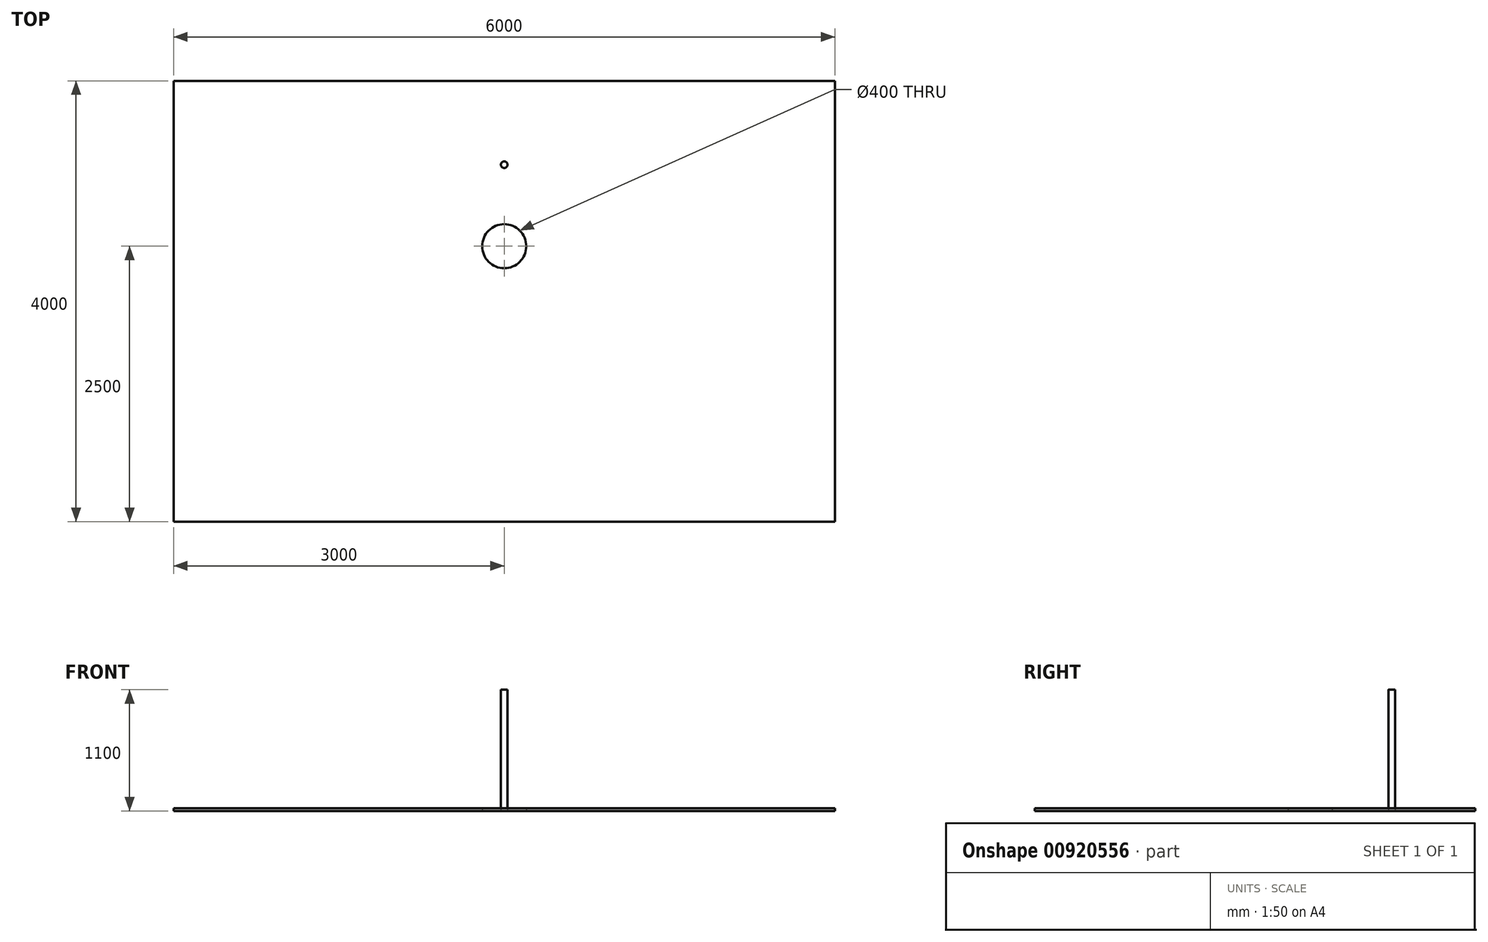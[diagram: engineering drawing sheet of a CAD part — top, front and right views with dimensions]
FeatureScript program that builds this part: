
annotation { "Feature Type Name" : "Feature", "Feature Type Description" : "" }
export const myFeature = defineFeature(function(context is Context, id is Id, definition is map)
    precondition{}
    {
        {
            var Q0;
            Q0=qCreatedBy(makeId("Top.planeOp"),FACE);
            var sketch = newSketch(context, id + "F0", { "sketchPlane" : qUnion([Q0])});
            skLineSegment(sketch, "E0.bottom", {"start": v(-3000, -3300) * mm, "end": v(3000, -3300) * mm});
            skLineSegment(sketch, "E0.top", {"start": v(-3000, 700) * mm, "end": v(3000, 700) * mm});
            skLineSegment(sketch, "E0.left", {"start": v(-3000, -3300) * mm, "end": v(-3000, 700) * mm});
            skLineSegment(sketch, "E0.right", {"start": v(3000, -3300) * mm, "end": v(3000, 700) * mm});
            skCircle(sketch, "E1", {"center": v(0, -800) * mm, "radius": 200 * mm});
            skSolve(sketch);
        }
        {
            var Q0;
            Q0 = qSketchRegion(id + "F0", true);
            extrude(context, id + "F1", {"entities" : qUnion([Q0]), "depth" : 25 * mm, "offsetDistance" : 25 * mm});
        }
        {
            var Q0;
            Q0=makeQuery(id+"F0.imprint","IMPRINT",FACE,{"disambiguationData":[TD([[makeQuery(id+"F0.imprint","IMPRINT",EDGE,{"derivedFrom":sQuery(id+"F0.wireOp",EDGE,"E0.bottom")}),1.0]])]});
            var sketch = newSketch(context, id + "F2", { "sketchPlane" : qUnion([Q0])});
            skCircle(sketch, "E2", {"center": v(0, -60) * mm, "radius": 30 * mm});
            skSolve(sketch);
        }
        {
            var Q0;
            Q0 = qSketchRegion(id + "F2", true);
            extrude(context, id + "F3", {"entities" : qUnion([Q0]), "depth" : 1100 * mm, "offsetDistance" : 25 * mm});
        }
    });
